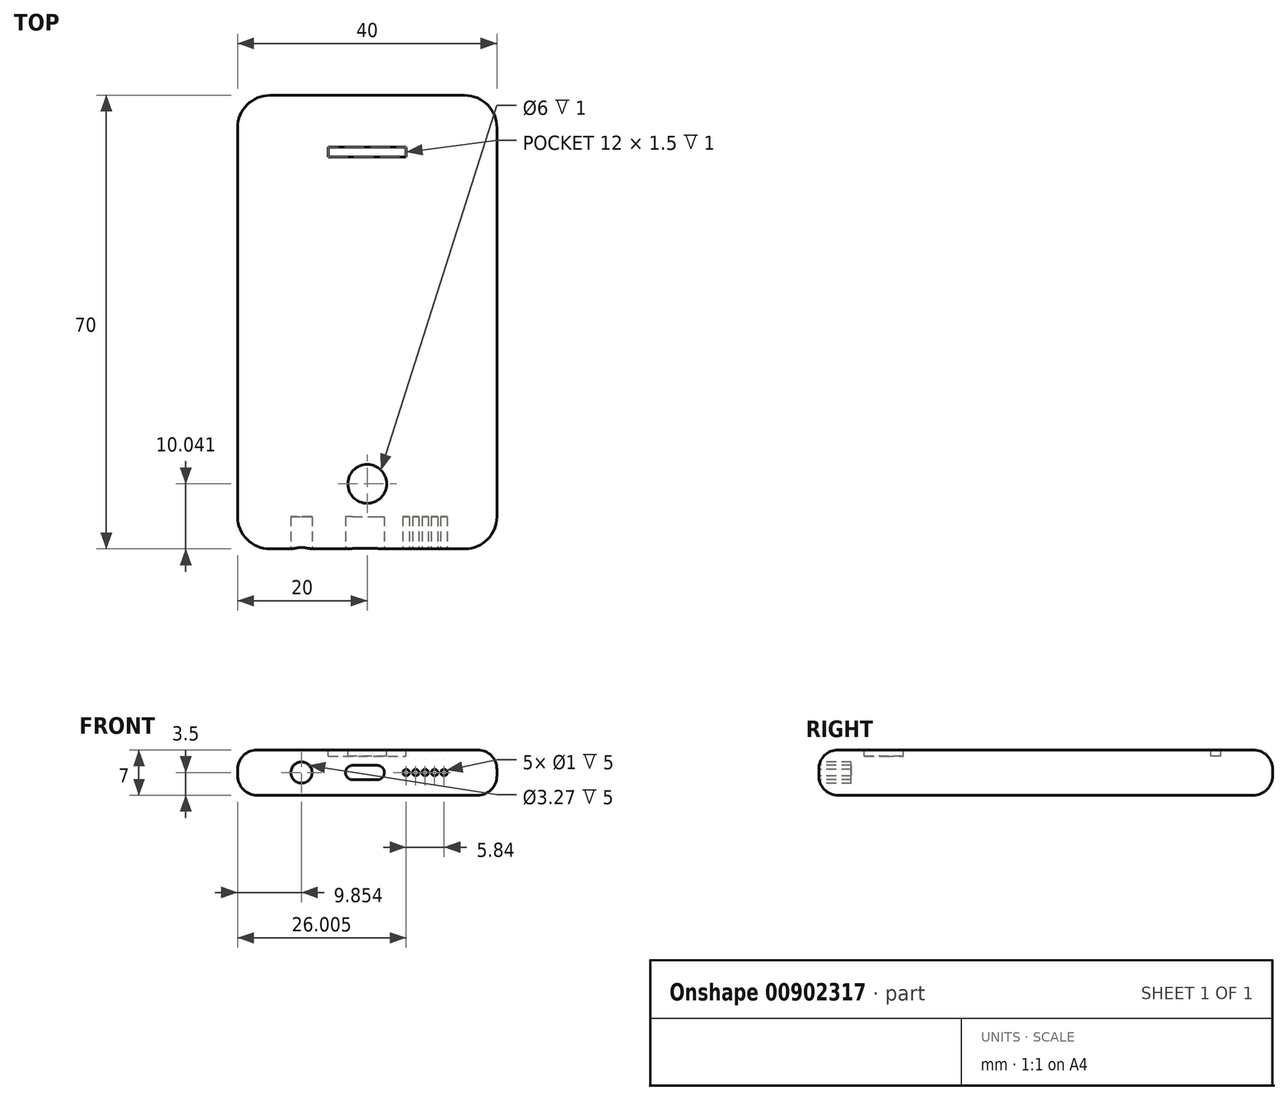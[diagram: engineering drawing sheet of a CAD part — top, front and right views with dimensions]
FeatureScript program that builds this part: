
annotation { "Feature Type Name" : "Feature", "Feature Type Description" : "" }
export const myFeature = defineFeature(function(context is Context, id is Id, definition is map)
    precondition{}
    {
        {
            var Q0;
            Q0=qCreatedBy(makeId("Top.planeOp"),FACE);
            var sketch = newSketch(context, id + "F0", { "sketchPlane" : qUnion([Q0])});
            skLineSegment(sketch, "E0.bottom", {"start": v(0, 0) * mm, "end": v(40, 0) * mm});
            skLineSegment(sketch, "E0.top", {"start": v(0, 70) * mm, "end": v(40, 70) * mm});
            skLineSegment(sketch, "E0.left", {"start": v(0, 0) * mm, "end": v(0, 70) * mm});
            skLineSegment(sketch, "E0.right", {"start": v(40, 0) * mm, "end": v(40, 70) * mm});
            skSolve(sketch);
        }
        {
            var Q0;
            Q0=makeQuery(id+"F0.imprint","IMPRINT",FACE,{"disambiguationData":[TD([[makeQuery(id+"F0.imprint","IMPRINT",EDGE,{"derivedFrom":sQuery(id+"F0.wireOp",EDGE,"E0.bottom")}),1.0]])]});
            extrude(context, id + "F1", {"entities" : qUnion([Q0]), "depth" : 7 * mm, "offsetDistance" : 25 * mm});
        }
        {
            var Q0;
            Q0=makeQuery(id+"F1.opExtrude","SWEPT_EDGE",EDGE,{"disambiguationData":[OSD([sQuery(id+"F0.wireOp",EDGE,"E0.bottom"),sQuery(id+"F0.wireOp",EDGE,"E0.right")])]});
            var Q1;
            Q1=makeQuery(id+"F1.opExtrude","SWEPT_EDGE",EDGE,{"disambiguationData":[OSD([sQuery(id+"F0.wireOp",EDGE,"E0.bottom"),sQuery(id+"F0.wireOp",EDGE,"E0.left")])]});
            var Q2;
            Q2=makeQuery(id+"F1.opExtrude","SWEPT_EDGE",EDGE,{"disambiguationData":[OSD([sQuery(id+"F0.wireOp",EDGE,"E0.top"),sQuery(id+"F0.wireOp",EDGE,"E0.right")])]});
            var Q3;
            Q3=makeQuery(id+"F1.opExtrude","SWEPT_EDGE",EDGE,{"disambiguationData":[OSD([sQuery(id+"F0.wireOp",EDGE,"E0.top"),sQuery(id+"F0.wireOp",EDGE,"E0.left")])]});
            fillet(context, id + "F2", {"entities" : qUnion([Q0, Q1, Q2, Q3]), "radius" : 5 * mm, "tangentPropagation" : true, "allowEdgeOverflow" : false});
        }
        {
            var Q0;
            Q0=makeQuery(id+"F1.opExtrude","SWEPT_FACE",FACE,{"disambiguationData":[OSD([sQuery(id+"F0.wireOp",EDGE,"E0.bottom")])]});
            var sketch = newSketch(context, id + "F3", { "sketchPlane" : qUnion([Q0])});
            skCircle(sketch, "E1", {"center": v(9.85, 3.5) * mm, "radius": 1.63 * mm});
            skPoint(sketch, "E1.centerSnap0", {"position": v(5, 3.5) * mm});
            skArc(sketch, "E2", {"start": v(17.75, 4.62) * mm, "mid": v(16.64, 3.5) * mm, "end": v(17.75, 2.38) * mm});
            skArc(sketch, "E3", {"start": v(21.53, 2.38) * mm, "mid": v(22.64, 3.5) * mm, "end": v(21.53, 4.62) * mm});
            skLineSegment(sketch, "E4", {"start": v(17.75, 4.62) * mm, "end": v(21.53, 4.62) * mm});
            skLineSegment(sketch, "E5", {"start": v(17.75, 2.38) * mm, "end": v(21.53, 2.38) * mm});
            skCircle(sketch, "E6", {"center": v(26, 3.5) * mm, "radius": 0.5 * mm});
            skCircle(sketch, "E7.1.0.0", {"center": v(27.47, 3.5) * mm, "radius": 0.5 * mm});
            skCircle(sketch, "E7.2.0.0", {"center": v(28.93, 3.5) * mm, "radius": 0.5 * mm});
            skCircle(sketch, "E7.3.0.0", {"center": v(30.39, 3.5) * mm, "radius": 0.5 * mm});
            skCircle(sketch, "E7.4.0.0", {"center": v(31.85, 3.5) * mm, "radius": 0.5 * mm});
            skLineSegment(sketch, "E7.direction1", {"start": v(26, 3.5) * mm, "end": v(27.47, 3.5) * mm, "construction": true});
            skSolve(sketch);
        }
        {
            var Q0;
            Q0=makeQuery(id+"F3.imprint","IMPRINT",FACE,{"disambiguationData":[TD([[makeQuery(id+"F3.imprint","IMPRINT",EDGE,{"derivedFrom":sQuery(id+"F3.wireOp",EDGE,"E2")}),1.0]])]});
            var Q1;
            Q1=makeQuery(id+"F3.imprint","IMPRINT",FACE,{"disambiguationData":[TD([[makeQuery(id+"F3.imprint","IMPRINT",EDGE,{"derivedFrom":sQuery(id+"F3.wireOp",EDGE,"E6")}),1.0]])]});
            var Q2;
            Q2=makeQuery(id+"F3.imprint","IMPRINT",FACE,{"disambiguationData":[TD([[makeQuery(id+"F3.imprint","IMPRINT",EDGE,{"derivedFrom":sQuery(id+"F3.wireOp",EDGE,"E7.1.0.0")}),1.0]])]});
            var Q3;
            Q3=makeQuery(id+"F3.imprint","IMPRINT",FACE,{"disambiguationData":[TD([[makeQuery(id+"F3.imprint","IMPRINT",EDGE,{"derivedFrom":sQuery(id+"F3.wireOp",EDGE,"E7.2.0.0")}),1.0]])]});
            var Q4;
            Q4=makeQuery(id+"F3.imprint","IMPRINT",FACE,{"disambiguationData":[TD([[makeQuery(id+"F3.imprint","IMPRINT",EDGE,{"derivedFrom":sQuery(id+"F3.wireOp",EDGE,"E7.3.0.0")}),1.0]])]});
            var Q5;
            Q5=makeQuery(id+"F3.imprint","IMPRINT",FACE,{"disambiguationData":[TD([[makeQuery(id+"F3.imprint","IMPRINT",EDGE,{"derivedFrom":sQuery(id+"F3.wireOp",EDGE,"E7.4.0.0")}),1.0]])]});
            var Q6;
            Q6=makeQuery(id+"F3.imprint","IMPRINT",FACE,{"disambiguationData":[TD([[makeQuery(id+"F3.imprint","IMPRINT",EDGE,{"derivedFrom":sQuery(id+"F3.wireOp",EDGE,"E1")}),1.0]])]});
            extrude(context, id + "F4", {"entities" : qUnion([Q0, Q1, Q2, Q3, Q4, Q5, Q6]), "operationType" : NewBodyOperationType.REMOVE, "oppositeDirection" : true, "depth" : 5 * mm, "offsetDistance" : 25 * mm});
        }
        {
            var Q0;
            Q0=makeQuery(id+"F1.opExtrude","CAP_EDGE",EDGE,{"disambiguationData":[OSD([sQuery(id+"F0.wireOp",EDGE,"E0.left")])],"isStart":false});
            var Q1;
            Q1=makeQuery(id+"F1.opExtrude","CAP_EDGE",EDGE,{"disambiguationData":[OSD([sQuery(id+"F0.wireOp",EDGE,"E0.left")])],"isStart":true});
            fillet(context, id + "F5", {"entities" : qUnion([Q0, Q1]), "radius" : 3 * mm, "tangentPropagation" : true, "allowEdgeOverflow" : false});
        }
        {
            var Q0;
            Q0=makeQuery(id+"F1.opExtrude","CAP_FACE",FACE,{"disambiguationData":[OSD([sQuery(id+"F0.wireOp",EDGE,"E0.bottom"),sQuery(id+"F0.wireOp",EDGE,"E0.top"),sQuery(id+"F0.wireOp",EDGE,"E0.left"),sQuery(id+"F0.wireOp",EDGE,"E0.right")])],"isStart":false});
            var sketch = newSketch(context, id + "F6", { "sketchPlane" : qUnion([Q0])});
            skLineSegment(sketch, "E8.bottom", {"start": v(14, 62) * mm, "end": v(26, 62) * mm});
            skLineSegment(sketch, "E8.top", {"start": v(14, 60.5) * mm, "end": v(26, 60.5) * mm});
            skLineSegment(sketch, "E8.left", {"start": v(14, 62) * mm, "end": v(14, 60.5) * mm});
            skLineSegment(sketch, "E8.right", {"start": v(26, 62) * mm, "end": v(26, 60.5) * mm});
            skCircle(sketch, "E9", {"center": v(20, 10.04) * mm, "radius": 3 * mm});
            skPoint(sketch, "E9.centerSnap0", {"position": v(20, 3) * mm});
            skSolve(sketch);
        }
        {
            var Q0;
            Q0=makeQuery(id+"F6.imprint","IMPRINT",FACE,{"disambiguationData":[TD([[makeQuery(id+"F6.imprint","IMPRINT",EDGE,{"derivedFrom":sQuery(id+"F6.wireOp",EDGE,"E9")}),1.0]])]});
            var Q1;
            Q1=makeQuery(id+"F6.imprint","IMPRINT",FACE,{"disambiguationData":[TD([[makeQuery(id+"F6.imprint","IMPRINT",EDGE,{"derivedFrom":sQuery(id+"F6.wireOp",EDGE,"E8.bottom")}),-1.0]])]});
            extrude(context, id + "F7", {"entities" : qUnion([Q0, Q1]), "operationType" : NewBodyOperationType.REMOVE, "oppositeDirection" : true, "depth" : 1 * mm, "offsetDistance" : 25 * mm});
        }
    });
